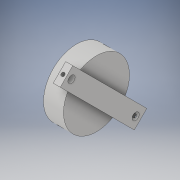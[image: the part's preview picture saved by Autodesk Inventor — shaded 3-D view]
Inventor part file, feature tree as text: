
AUTODESK INVENTOR PART (.ipt)
format: ipt  version: 2019 (Build 230136000, 136)  size: 281,088 bytes
history: native  units: in
note: dims shown in document units (in); Inventor stores cm internally (conversion verified against a paired STEP export)
features: sketch x13, extrude x11, plane x4, mirror x3, thread x2, pattern_circular x1, projected_geometry x1
ambient origin geometry x8: Origin, YZ Plane, XZ Plane, XY Plane, X Axis, Y Axis, Z Axis, Center Point
bodies: Solid1 (feature_tree), Solid2 (feature_tree)
feature tree (35):
  extrude  "Extrusion1"  Depth=1.7323in
  extrude  "Extrusion3"  Depth=1.2402in
  extrude  "Extrusion4"  Depth=1.1811in TaperAngle=0.0deg
  pattern_circular  "Circular Pattern1"  Count=4 Angle=360.0deg
  sketch  "Sketch6"  dims[d16=0.3937in d17=45.0deg]
  plane  "Work Plane1"
  extrude  "Extrusion5"  TaperAngle=45.0deg  [1 undecoded]
  plane  "Work Plane2"
  mirror  "Mirror1"
  extrude  "Extrusion6"  TaperAngle=45.0deg  [1 undecoded]
  extrude  "Extrusion7"  Depth=0.2362in TaperAngle=0.0deg
  sketch  "Sketch11"  dims[d26=0.3937in d27=0.0in d28=0.0118in]
  plane  "Work Plane3"
  extrude  "Extrusion8"  TaperAngle=45.0deg  [1 undecoded]
  thread  "Thread1"  [1 undecoded]
  mirror  "Mirror2"
  extrude  "Extrusion9"  Depth=0.3937in
  extrude  "Extrusion14"  Depth=0.2362in
  extrude  "Extrusion15"  Depth=0.0098in
  extrude  "Extrusion16"  Depth=0.4724in
  thread  "Thread3"  [1 undecoded]
  plane  "Work Plane5"
  mirror  "Mirror3"
  sketch  "Sketch2"  dims[d3=0.7874in d4=1.7323in]
  sketch  "Sketch4"  dims[d5=0.4724in d6=0.0in d9=1.2402in]
  sketch  "Sketch5"  dims[d10=0.2008in d11=1.1811in d12=0.0in d13=1.5748in d14=360.0deg]
  sketch  "Sketch7"  dims[d18=0.1181in d19=45.0deg]
  sketch  "Sketch8"  dims[d20=0.3543in d21=0.2362in d22=0.0in]
  projected_geometry  "Projected Loop1"
  sketch  "Sketch9"  dims[d23=0.8661in d24=45.0deg d25=0.2047in]
  sketch  "Sketch12"  dims[d29=0.4724in d30=0.0in d31=0.2362in]
  sketch  "Sketch13"  dims[d32=0.4724in d33=0.0in d34=0.0098in]
  sketch  "Sketch22"  dims[d35=45.0deg d36=0.4724in d37=0.1969in]
  sketch  "Sketch23"  dims[d38=0.3937in d39=0.0in]
  sketch  "Sketch24"  dims[d40=0.3937in d41=0.0in d42=0.1969in d43=0.0in d73=3.5039in d74=225.0deg d75=0.5906in d76=0.2362in d77=0.0in d78=0.2362in d79=45.0deg d80=0.2402in d81=0.2047in d82=0.0in d83=0.1181in d84=0.2047in d85=0.0in d86=0.3937in d87=0.0in]
note: 5 required parameter values undecoded (feature->parameter linkage not recoverable at this tier; creation-order binding heuristic only, values carry confidence <= 0.55)
